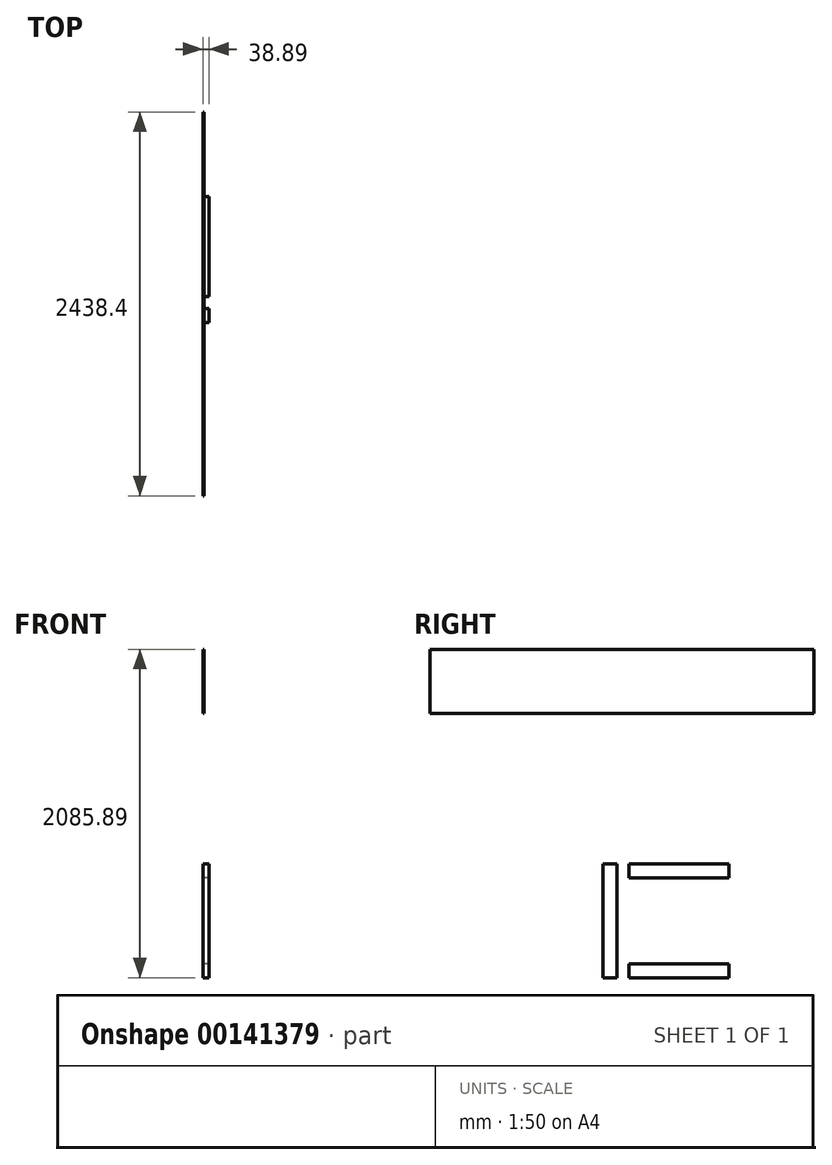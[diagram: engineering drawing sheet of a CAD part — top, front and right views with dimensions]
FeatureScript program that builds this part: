
annotation { "Feature Type Name" : "Feature", "Feature Type Description" : "" }
export const myFeature = defineFeature(function(context is Context, id is Id, definition is map)
    precondition{}
    {
        {
            var Q0;
            Q0=qCreatedBy(makeId("Right.planeOp"),FACE);
            var sketch = newSketch(context, id + "F0", { "sketchPlane" : qUnion([Q0])});
            skLineSegment(sketch, "E0", {"start": v(-477.73, 245.42) * mm, "end": v(-477.73, -478.48) * mm});
            skLineSegment(sketch, "E1", {"start": v(-312.63, -478.48) * mm, "end": v(322.37, -478.48) * mm});
            skLineSegment(sketch, "E2", {"start": v(322.37, -389.58) * mm, "end": v(322.37, -478.48) * mm});
            skLineSegment(sketch, "E3", {"start": v(-477.73, 245.42) * mm, "end": v(-388.83, 245.42) * mm});
            skLineSegment(sketch, "E4", {"start": v(322.37, -389.58) * mm, "end": v(-312.63, -389.58) * mm});
            skLineSegment(sketch, "E5.bottom", {"start": v(-312.63, 245.42) * mm, "end": v(322.37, 245.42) * mm});
            skLineSegment(sketch, "E5.top", {"start": v(-312.63, 156.52) * mm, "end": v(322.37, 156.52) * mm});
            skLineSegment(sketch, "E5.left", {"start": v(-312.63, 245.42) * mm, "end": v(-312.63, 156.52) * mm});
            skLineSegment(sketch, "E5.right", {"start": v(322.37, 245.42) * mm, "end": v(322.37, 156.52) * mm});
            skLineSegment(sketch, "E6", {"start": v(-312.63, -389.58) * mm, "end": v(-312.63, -478.48) * mm});
            skLineSegment(sketch, "E7", {"start": v(-388.83, 245.42) * mm, "end": v(-388.83, -478.48) * mm});
            skLineSegment(sketch, "E8", {"start": v(-388.83, -478.48) * mm, "end": v(-477.73, -478.48) * mm});
            skSolve(sketch);
        }
        {
            var Q0;
            Q0 = qSketchRegion(id + "F0", true);
            extrude(context, id + "F1", {"entities" : qUnion([Q0]), "depth" : 38.1 * mm});
        }
        {
            var Q0;
            Q0=qCreatedBy(makeId("Right.planeOp"),FACE);
            var sketch = newSketch(context, id + "F2", { "sketchPlane" : qUnion([Q0])});
            skLineSegment(sketch, "E9.bottom", {"start": v(-1578.34, 1607.41) * mm, "end": v(860.06, 1607.41) * mm});
            skLineSegment(sketch, "E9.top", {"start": v(-1578.34, 1201.01) * mm, "end": v(860.06, 1201.01) * mm});
            skLineSegment(sketch, "E9.left", {"start": v(-1578.34, 1607.41) * mm, "end": v(-1578.34, 1201.01) * mm});
            skLineSegment(sketch, "E9.right", {"start": v(860.06, 1607.41) * mm, "end": v(860.06, 1201.01) * mm});
            skSolve(sketch);
        }
        {
            var Q0;
            Q0 = qSketchRegion(id + "F2", true);
            extrude(context, id + "F3", {"entities" : qUnion([Q0]), "depth" : 6.35 * mm});
        }
        {
            var Q0;
            Q0=makeQuery(id+"F3.opExtrude","CAP_FACE",FACE,{"disambiguationData":[OSD([sQuery(id+"F2.wireOp",EDGE,"E9.bottom"),sQuery(id+"F2.wireOp",EDGE,"E9.top"),sQuery(id+"F2.wireOp",EDGE,"E9.left"),sQuery(id+"F2.wireOp",EDGE,"E9.right")])],"isStart":false});
            var sketch = newSketch(context, id + "F4", { "sketchPlane" : qUnion([Q0])});
            skLineSegment(sketch, "E10.bottom", {"start": v(-1578.34, 1607.41) * mm, "end": v(860.06, 1607.41) * mm});
            skLineSegment(sketch, "E10.top", {"start": v(-1578.34, 1201.01) * mm, "end": v(860.06, 1201.01) * mm});
            skLineSegment(sketch, "E10.left", {"start": v(-1578.34, 1810.61) * mm, "end": v(-1578.34, 1201.01) * mm});
            skLineSegment(sketch, "E10.right", {"start": v(860.06, 1607.41) * mm, "end": v(860.06, 1201.01) * mm});
            skSolve(sketch);
        }
        {
            var Q0;
            Q0 = qSketchRegion(id + "F4", true);
            var Q1;
            Q1=sQuery(id+"F4.wireOp",EDGE,"E10.bottom");
            extrude(context, id + "F5", {"entities" : qUnion([Q0]), "surfaceEntities" : qUnion([Q1]), "depth" : 0.8 * mm});
        }
        {
            var Q0;
            Q0=makeQuery(id+"F3.opExtrude","CAP_FACE",FACE,{"disambiguationData":[OSD([sQuery(id+"F2.wireOp",EDGE,"E9.bottom"),sQuery(id+"F2.wireOp",EDGE,"E9.top"),sQuery(id+"F2.wireOp",EDGE,"E9.left"),sQuery(id+"F2.wireOp",EDGE,"E9.right")])],"isStart":true});
            var sketch = newSketch(context, id + "F6", { "sketchPlane" : qUnion([Q0])});
            skLineSegment(sketch, "E11.bottom", {"start": v(-860.06, 1607.41) * mm, "end": v(1578.34, 1607.41) * mm});
            skLineSegment(sketch, "E11.top", {"start": v(-860.06, 1201.01) * mm, "end": v(1578.34, 1201.01) * mm});
            skLineSegment(sketch, "E11.left", {"start": v(-860.06, 1607.41) * mm, "end": v(-860.06, 1201.01) * mm});
            skLineSegment(sketch, "E11.right", {"start": v(1578.34, 1607.41) * mm, "end": v(1578.34, 1201.01) * mm});
            skSolve(sketch);
        }
        {
            var Q0;
            Q0 = qSketchRegion(id + "F6", true);
            extrude(context, id + "F7", {"entities" : qUnion([Q0]), "depth" : 0.8 * mm});
        }
    });
